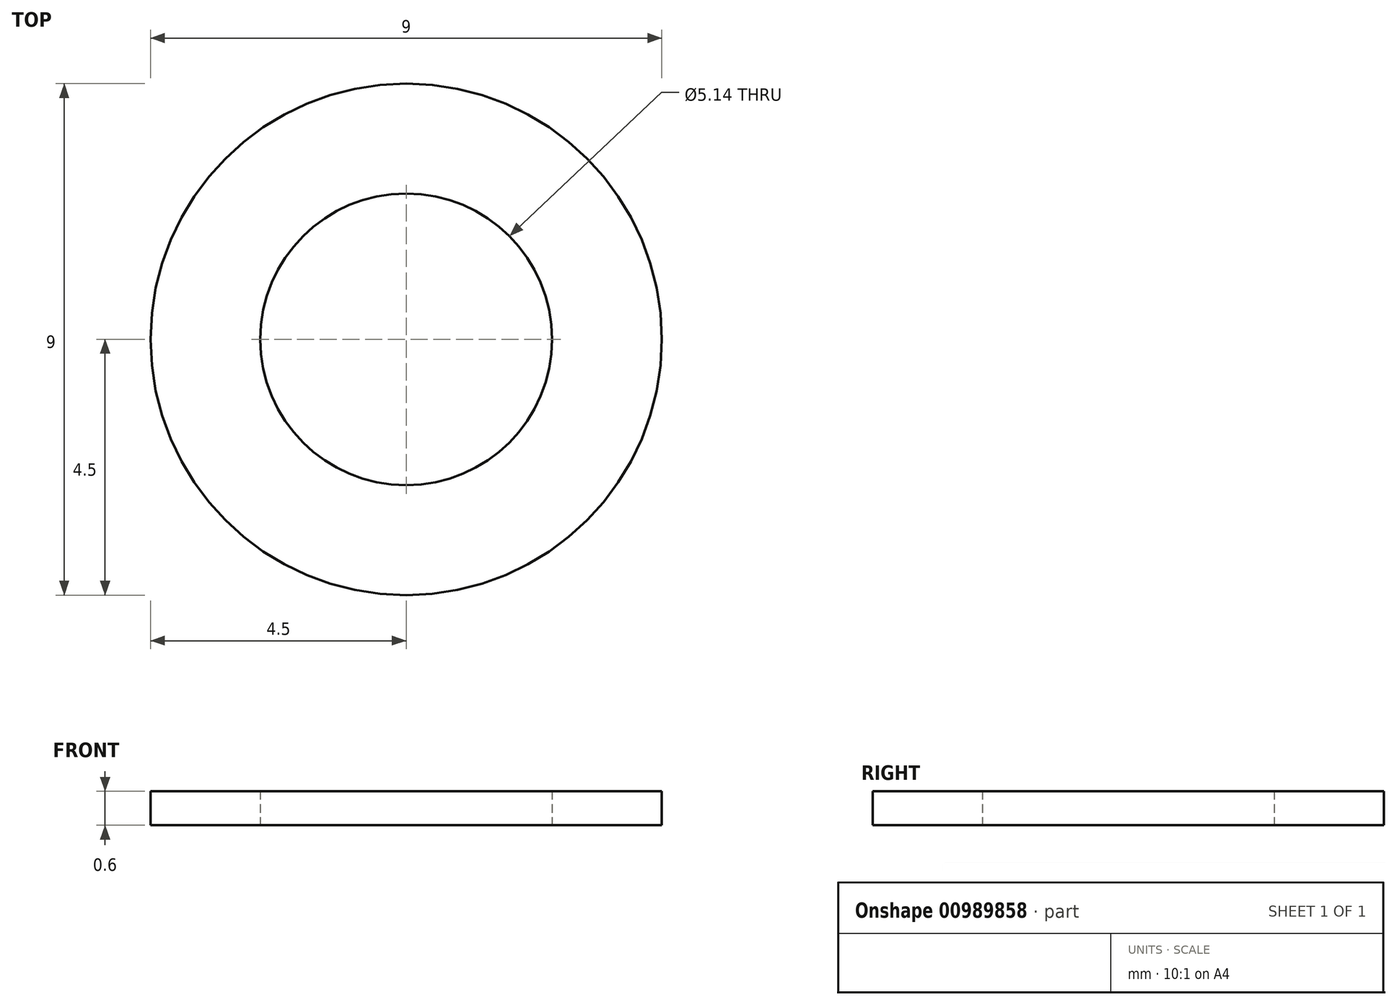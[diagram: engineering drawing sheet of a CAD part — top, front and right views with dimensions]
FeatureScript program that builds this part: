
annotation { "Feature Type Name" : "Feature", "Feature Type Description" : "" }
export const myFeature = defineFeature(function(context is Context, id is Id, definition is map)
    precondition{}
    {
        {
            var Q0;
            Q0=qCreatedBy(makeId("Top.planeOp"),FACE);
            var sketch = newSketch(context, id + "F0", { "sketchPlane" : qUnion([Q0])});
            skCircle(sketch, "E0", {"center": v(0, 0) * mm, "radius": 4.5 * mm});
            skCircle(sketch, "E1", {"center": v(0, 0) * mm, "radius": 2.57 * mm});
            skSolve(sketch);
        }
        {
            var Q0;
            Q0 = qSketchRegion(id + "F0", true);
            extrude(context, id + "F1", {"entities" : qUnion([Q0]), "flatOperationType" : FlatOperationType.REMOVE, "depth" : 0.6 * mm, "offsetDistance" : 25 * mm, "domain" : OperationDomain.MODEL});
        }
    });
